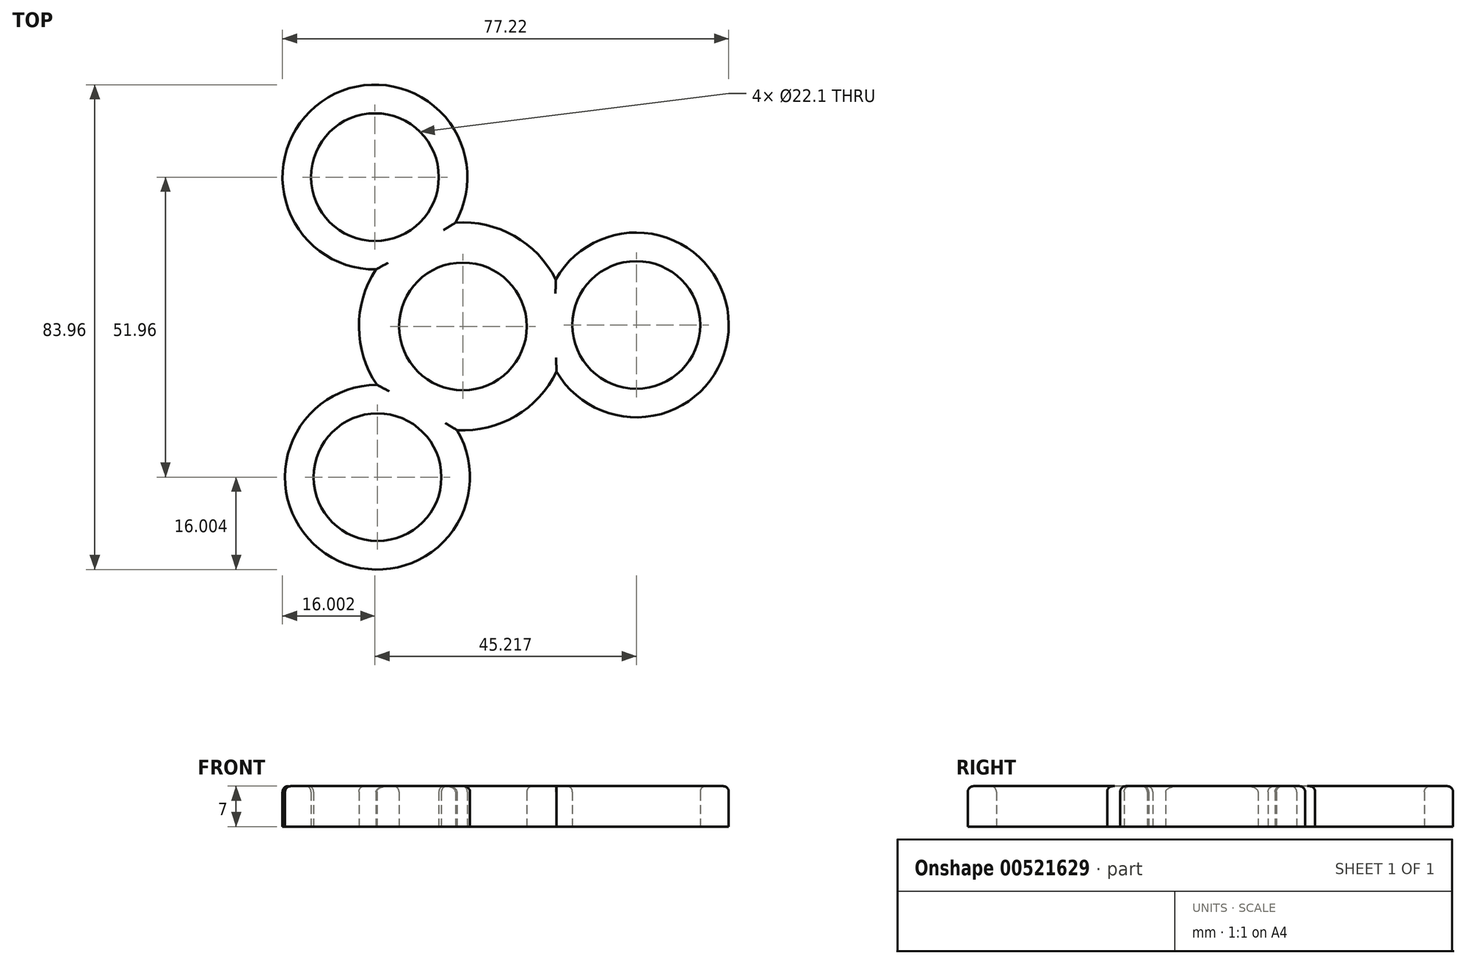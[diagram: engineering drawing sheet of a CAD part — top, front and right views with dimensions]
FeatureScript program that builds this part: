
annotation { "Feature Type Name" : "Feature", "Feature Type Description" : "" }
export const myFeature = defineFeature(function(context is Context, id is Id, definition is map)
    precondition{}
    {
        {
            var Q0;
            Q0=qCreatedBy(makeId("Top.planeOp"),FACE);
            var sketch = newSketch(context, id + "F0", { "sketchPlane" : qUnion([Q0])});
            skCircle(sketch, "E0", {"center": v(0, 0) * mm, "radius": 11.05 * mm});
            skCircle(sketch, "E1", {"center": v(0, 0) * mm, "radius": 18 * mm});
            skCircle(sketch, "E2", {"center": v(-15.22, 25.85) * mm, "radius": 11.05 * mm});
            skCircle(sketch, "E3", {"center": v(-14.78, -26.1) * mm, "radius": 11.05 * mm});
            skCircle(sketch, "E4", {"center": v(30, 0.25) * mm, "radius": 11.05 * mm});
            skCircle(sketch, "E5", {"center": v(-14.78, -26.1) * mm, "radius": 16 * mm});
            skCircle(sketch, "E6", {"center": v(-15.22, 25.85) * mm, "radius": 16 * mm});
            skCircle(sketch, "E7", {"center": v(30, 0.25) * mm, "radius": 16 * mm});
            skSolve(sketch);
        }
        {
            var Q0;
            {var subQ0=sQuery(id+"F0.wireOp",EDGE,"e9zcL3uG-clMW-CB6R-mPn1-NTrwoYadkIhf");var subQ1=sQuery(id+"F0.wireOp",EDGE,"E0");var subQ2=makeQuery(id+"F0.imprint","INTERSECT",VERTEX,{"derivedFrom":[subQ1,subQ0]});Q0=makeQuery(id+"F0.imprint","IMPRINT",FACE,{"disambiguationData":[TD([[makeQuery(id+"F0.imprint","IMPRINT",EDGE,{"disambiguationData":[TD([[subQ2,-1.0]])],"derivedFrom":subQ1}),-1.0]])]});}
            var Q1;
            Q1=makeQuery(id+"F0.imprint","IMPRINT",FACE,{"disambiguationData":[TD([[makeQuery(id+"F0.imprint","IMPRINT",EDGE,{"derivedFrom":sQuery(id+"F0.wireOp",EDGE,"E3")}),-1.0]])]});
            var Q2;
            {var subQ0=sQuery(id+"F0.wireOp",EDGE,"fM1NJ59R-5Gtm-2Vz8-hERX-S4Y3RQeVmU9U");var subQ1=sQuery(id+"F0.wireOp",EDGE,"E1");var subQ2=makeQuery(id+"F0.imprint","INTERSECT",VERTEX,{"derivedFrom":[subQ1,subQ0]});Q2=makeQuery(id+"F0.imprint","IMPRINT",FACE,{"disambiguationData":[TD([[makeQuery(id+"F0.imprint","IMPRINT",EDGE,{"disambiguationData":[TD([[subQ2,-1.0]])],"derivedFrom":subQ1}),-1.0]])]});}
            var Q3;
            {var subQ0=sQuery(id+"F0.wireOp",EDGE,"oOAs71K8-LSWc-4CLp-Zzfn-c75iS4tNiohm");var subQ1=sQuery(id+"F0.wireOp",EDGE,"E0");var subQ2=makeQuery(id+"F0.imprint","INTERSECT",VERTEX,{"derivedFrom":[subQ1,subQ0]});Q3=makeQuery(id+"F0.imprint","IMPRINT",FACE,{"disambiguationData":[TD([[makeQuery(id+"F0.imprint","IMPRINT",EDGE,{"disambiguationData":[TD([[subQ2,1.0]])],"derivedFrom":subQ1}),-1.0]])]});}
            var Q4;
            {var subQ1=sQuery(id+"F0.wireOp",EDGE,"E1");var subQ3=sQuery(id+"F0.wireOp",EDGE,"jgwlEjWp-sw9u-VY17-f9nH-SewB5XZ8HkPX");var subQ4=makeQuery(id+"F0.imprint","INTERSECT",VERTEX,{"derivedFrom":[subQ1,subQ3]});Q4=makeQuery(id+"F0.imprint","IMPRINT",FACE,{"disambiguationData":[TD([[makeQuery(id+"F0.imprint","IMPRINT",EDGE,{"disambiguationData":[TD([[subQ4,1.0]])],"derivedFrom":subQ3}),1.0]])]});}
            var Q5;
            {var subQ0=sQuery(id+"F0.wireOp",EDGE,"e9zcL3uG-clMW-CB6R-mPn1-NTrwoYadkIhf");var subQ1=sQuery(id+"F0.wireOp",EDGE,"E0");var subQ2=makeQuery(id+"F0.imprint","INTERSECT",VERTEX,{"derivedFrom":[subQ1,subQ0]});Q5=makeQuery(id+"F0.imprint","IMPRINT",FACE,{"disambiguationData":[TD([[makeQuery(id+"F0.imprint","IMPRINT",EDGE,{"disambiguationData":[TD([[subQ2,1.0]])],"derivedFrom":subQ1}),-1.0]])]});}
            var Q6;
            {var subQ1=sQuery(id+"F0.wireOp",EDGE,"E1");var subQ3=sQuery(id+"F0.wireOp",EDGE,"oOAs71K8-LSWc-4CLp-Zzfn-c75iS4tNiohm");var subQ4=makeQuery(id+"F0.imprint","INTERSECT",VERTEX,{"derivedFrom":[subQ1,subQ3]});Q6=makeQuery(id+"F0.imprint","IMPRINT",FACE,{"disambiguationData":[TD([[makeQuery(id+"F0.imprint","IMPRINT",EDGE,{"disambiguationData":[TD([[subQ4,1.0]])],"derivedFrom":subQ3}),1.0]])]});}
            var Q7;
            Q7=makeQuery(id+"F0.imprint","IMPRINT",FACE,{"disambiguationData":[TD([[makeQuery(id+"F0.imprint","IMPRINT",EDGE,{"derivedFrom":sQuery(id+"F0.wireOp",EDGE,"E4")}),-1.0]])]});
            var Q8;
            Q8=makeQuery(id+"F0.imprint","IMPRINT",FACE,{"disambiguationData":[TD([[makeQuery(id+"F0.imprint","IMPRINT",EDGE,{"derivedFrom":sQuery(id+"F0.wireOp",EDGE,"E2")}),-1.0]])]});
            var Q9;
            {var subQ0=sQuery(id+"F0.wireOp",EDGE,"iWpcJYMW-lp7D-Rta9-vDUY-uTJnxPVIUKOB");var subQ1=sQuery(id+"F0.wireOp",EDGE,"E1");var subQ2=makeQuery(id+"F0.imprint","INTERSECT",VERTEX,{"derivedFrom":[subQ1,subQ0]});Q9=makeQuery(id+"F0.imprint","IMPRINT",FACE,{"disambiguationData":[TD([[makeQuery(id+"F0.imprint","IMPRINT",EDGE,{"disambiguationData":[TD([[subQ2,-1.0]])],"derivedFrom":subQ1}),-1.0]])]});}
            var Q10;
            {var subQ0=sQuery(id+"F0.wireOp",EDGE,"nEZrQKPM-t3Dd-AM5R-DWg6-JUV7cxrYPtug");var subQ1=sQuery(id+"F0.wireOp",EDGE,"E1");var subQ2=makeQuery(id+"F0.imprint","INTERSECT",VERTEX,{"derivedFrom":[subQ1,subQ0]});Q10=makeQuery(id+"F0.imprint","IMPRINT",FACE,{"disambiguationData":[TD([[makeQuery(id+"F0.imprint","IMPRINT",EDGE,{"disambiguationData":[TD([[subQ2,-1.0]])],"derivedFrom":subQ1}),-1.0]])]});}
            var Q11;
            {var subQ0=sQuery(id+"F0.wireOp",EDGE,"oOAs71K8-LSWc-4CLp-Zzfn-c75iS4tNiohm");var subQ1=sQuery(id+"F0.wireOp",EDGE,"E1");var subQ2=makeQuery(id+"F0.imprint","INTERSECT",VERTEX,{"derivedFrom":[subQ1,subQ0]});Q11=makeQuery(id+"F0.imprint","IMPRINT",FACE,{"disambiguationData":[TD([[makeQuery(id+"F0.imprint","IMPRINT",EDGE,{"disambiguationData":[TD([[subQ2,1.0]])],"derivedFrom":subQ1}),1.0]])]});}
            var Q12;
            {var subQ0=sQuery(id+"F0.wireOp",EDGE,"jgwlEjWp-sw9u-VY17-f9nH-SewB5XZ8HkPX");var subQ1=sQuery(id+"F0.wireOp",EDGE,"E1");var subQ2=makeQuery(id+"F0.imprint","INTERSECT",VERTEX,{"derivedFrom":[subQ1,subQ0]});Q12=makeQuery(id+"F0.imprint","IMPRINT",FACE,{"disambiguationData":[TD([[makeQuery(id+"F0.imprint","IMPRINT",EDGE,{"disambiguationData":[TD([[subQ2,1.0]])],"derivedFrom":subQ1}),1.0]])]});}
            var Q13;
            {var subQ1=sQuery(id+"F0.wireOp",EDGE,"E1");var subQ3=sQuery(id+"F0.wireOp",EDGE,"e9zcL3uG-clMW-CB6R-mPn1-NTrwoYadkIhf");var subQ4=makeQuery(id+"F0.imprint","INTERSECT",VERTEX,{"derivedFrom":[subQ1,subQ3]});Q13=makeQuery(id+"F0.imprint","IMPRINT",FACE,{"disambiguationData":[TD([[makeQuery(id+"F0.imprint","IMPRINT",EDGE,{"disambiguationData":[TD([[subQ4,1.0]])],"derivedFrom":subQ3}),1.0]])]});}
            var Q14;
            {var subQ0=sQuery(id+"F0.wireOp",EDGE,"e9zcL3uG-clMW-CB6R-mPn1-NTrwoYadkIhf");var subQ1=sQuery(id+"F0.wireOp",EDGE,"E1");var subQ2=makeQuery(id+"F0.imprint","INTERSECT",VERTEX,{"derivedFrom":[subQ1,subQ0]});Q14=makeQuery(id+"F0.imprint","IMPRINT",FACE,{"disambiguationData":[TD([[makeQuery(id+"F0.imprint","IMPRINT",EDGE,{"disambiguationData":[TD([[subQ2,1.0]])],"derivedFrom":subQ1}),1.0]])]});}
            var Q15;
            {var subQ0=sQuery(id+"F0.wireOp",EDGE,"E5");var subQ1=sQuery(id+"F0.wireOp",EDGE,"E1");var subQ2=makeQuery(id+"F0.imprint","INTERSECT",VERTEX,{"disambiguationData":[OD(0.0)],"derivedFrom":[subQ1,subQ0]});Q15=makeQuery(id+"F0.imprint","IMPRINT",FACE,{"disambiguationData":[TD([[makeQuery(id+"F0.imprint","IMPRINT",EDGE,{"disambiguationData":[TD([[subQ2,-1.0]])],"derivedFrom":subQ1}),1.0]])]});}
            var Q16;
            {var subQ0=sQuery(id+"F0.wireOp",EDGE,"E6");var subQ1=sQuery(id+"F0.wireOp",EDGE,"E1");var subQ2=makeQuery(id+"F0.imprint","INTERSECT",VERTEX,{"disambiguationData":[OD(0.0)],"derivedFrom":[subQ1,subQ0]});Q16=makeQuery(id+"F0.imprint","IMPRINT",FACE,{"disambiguationData":[TD([[makeQuery(id+"F0.imprint","IMPRINT",EDGE,{"disambiguationData":[TD([[subQ2,-1.0]])],"derivedFrom":subQ1}),1.0]])]});}
            var Q17;
            {var subQ0=sQuery(id+"F0.wireOp",EDGE,"E7");var subQ1=sQuery(id+"F0.wireOp",EDGE,"E1");var subQ2=makeQuery(id+"F0.imprint","INTERSECT",VERTEX,{"disambiguationData":[OD(0.0)],"derivedFrom":[subQ1,subQ0]});Q17=makeQuery(id+"F0.imprint","IMPRINT",FACE,{"disambiguationData":[TD([[makeQuery(id+"F0.imprint","IMPRINT",EDGE,{"disambiguationData":[TD([[subQ2,1.0]])],"derivedFrom":subQ1}),1.0]])]});}
            extrude(context, id + "F1", {"entities" : qUnion([Q0, Q1, Q2, Q3, Q4, Q5, Q6, Q7, Q8, Q9, Q10, Q11, Q12, Q13, Q14, Q15, Q16, Q17]), "depth" : 7 * mm, "offsetDistance" : 25 * mm});
        }
        {
            var Q0;
            Q0=makeQuery(id+"F1.opExtrude","CAP_FACE",FACE,{"disambiguationData":[OSD([sQuery(id+"F0.wireOp",EDGE,"E0"),sQuery(id+"F0.wireOp",EDGE,"E2"),sQuery(id+"F0.wireOp",EDGE,"E3"),sQuery(id+"F0.wireOp",EDGE,"E4"),sQuery(id+"F0.wireOp",EDGE,"E5"),sQuery(id+"F0.wireOp",EDGE,"E6"),sQuery(id+"F0.wireOp",EDGE,"E7"),sQuery(id+"F0.wireOp",EDGE,"iWpcJYMW-lp7D-Rta9-vDUY-uTJnxPVIUKOB"),sQuery(id+"F0.wireOp",EDGE,"fM1NJ59R-5Gtm-2Vz8-hERX-S4Y3RQeVmU9U"),sQuery(id+"F0.wireOp",EDGE,"nEZrQKPM-t3Dd-AM5R-DWg6-JUV7cxrYPtug")])],"isStart":false});
            fillet(context, id + "F2", {"entities" : qUnion([Q0]), "radius" : 1 * mm, "tangentPropagation" : true, "allowEdgeOverflow" : false});
        }
    });
